# Revit family: WC-GBG-Nautic_HF_1500-Floor_Standing
name_source: partatom
category: Plumbing Fixtures
units: mm (PartAtom-declared; Revit-internal decimal feet)

## family parameters
Always vertical = Yes
Cut with Voids When Loaded = No
OmniClass Number = 23.45.05.21.11
OmniClass Title = Water Closets
Part Type = Normal
Room Calculation Point = No
Round Connector Dimension = Use Radius
Shared = No
Work Plane-Based = No

## types (1)
- Hard seat, Duo flush, C+
    Article Number = GB1115002R1321G
    Assembly Code = D2010100
    BIMobject category = WC
    Care Instruction URL = http://www.gustavsberg.com
    Code EAN = -
    Code LVI FIN = -
    Code NRF NOR = -
    Code RSK SWE = -
    Code VVS DNK = -
    Cold Water Connection Diameter = 15 mm  [stored 0.0492126 ft]
    Cold Water Connection Height = 360 mm
    Cold Water Connection Radius = 8 mm  [stored 0.0262467 ft]
    Default Elevation = 0 mm  [stored 0 ft]
    Description = 1500 Nautic HF WC with concealed S-trap for floor installation
    Design country = Sweden
    EAN code = https://4051202357107
    Edition number = 1
    Flush Rate = 4/2L
    Height = 800 mm  [stored 2.62467 ft]
    Installation Instruction URL = http://www.gustavsberg.com
    Installation instructions = http://www.gustavsberg.com
    Length = 700 mm
    Manufacturer = Villeroy & Boch Gustavsberg AB
    Manufacturer country = Sweden
    Manufacturer name = Gustavsberg
    Material = Gustavsberg Porcelain - White (with C+)
    Material main = Porcelain
    Material secondary = Plastic
    Model = 1500
    Nominal Flow = 0.1 L/s
    Nominal height = 0
    Nominal width = 0
    Pressure Drop = 130.0 Pa
    Product Guid = fdffca94-abd0-478c-b202-6e18a21e0884
    Product Page URL = http://www.gustavsberg.com
    Product SKU = GB111500
    Product certification = http://www.gustavsberg.com
    Product data url = https://bimobject.com
    Product family = Nautic
    Product group = Toilet
    QR code = http://bimobject.com
    Seat = Yes
    Seat Height = 420 mm
    Type Comments = 1500 WC Nautic HF 2/4 C+ w. Hard seat
    UNSPSC Code = 30181505
    URL = http://www.gustavsberg.com
    Waste Connection = Yes
    Waste Connection Diameter = 110 mm  [stored 0.360892 ft]
    Waste Connection Radius = 55 mm  [stored 0.180446 ft]
    Waste Connection Rough In = 75 mm
    Weight Net (Kg) = 0
    Width = 345 mm

note: [stored X ft] marks values corroborated as IEEE doubles in the binary element streams (Revit-internal decimal feet)

## geometry (parser evidence)
native form markers: Blend x8, Sweep x2
no freeform markers — native parametric forms only
